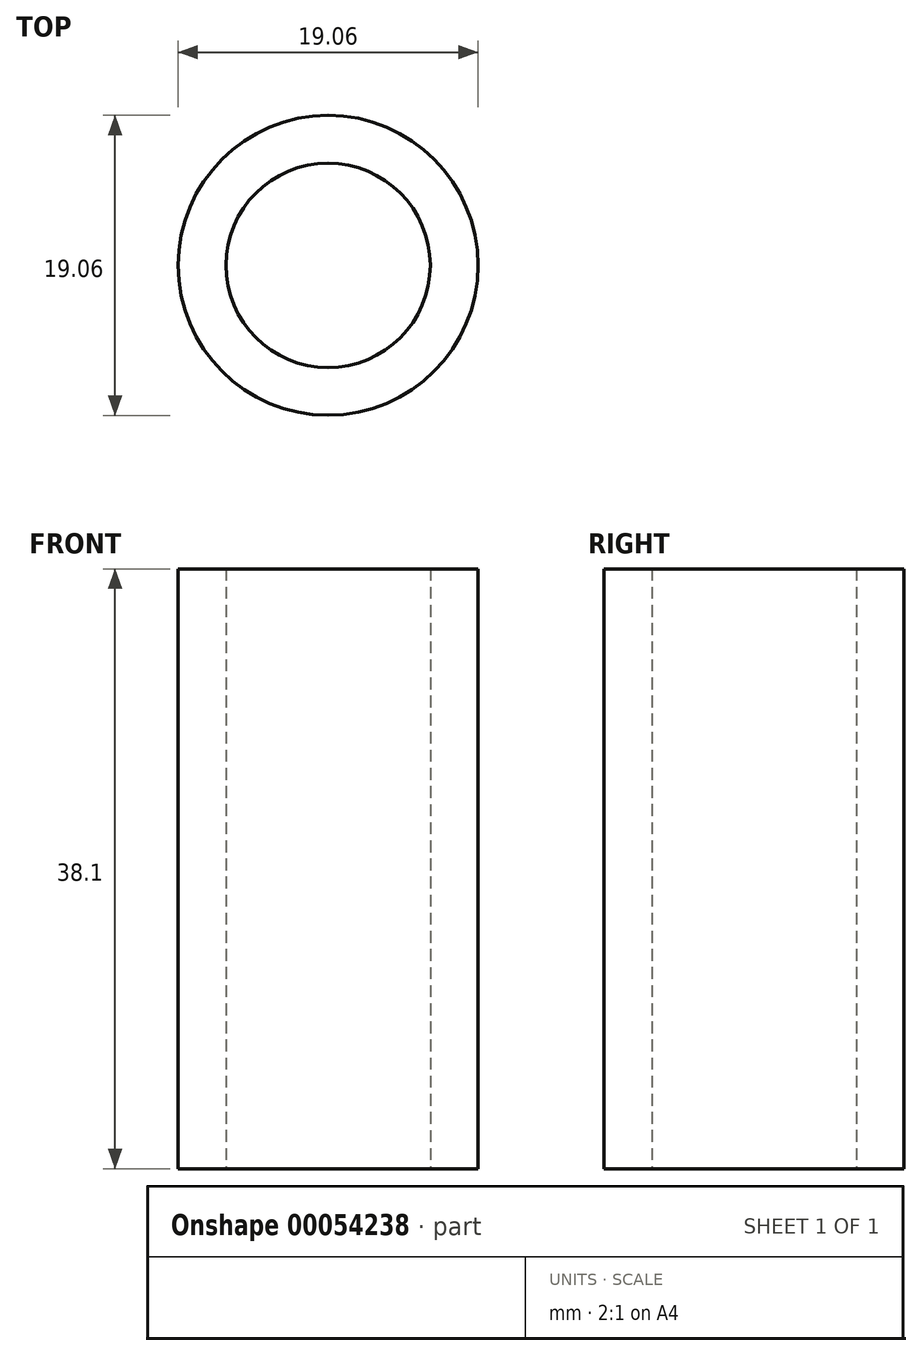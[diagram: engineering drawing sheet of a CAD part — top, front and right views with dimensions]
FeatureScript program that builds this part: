
annotation { "Feature Type Name" : "Feature", "Feature Type Description" : "" }
export const myFeature = defineFeature(function(context is Context, id is Id, definition is map)
    precondition{}
    {
        {
            var Q0;
            Q0=qCreatedBy(makeId("Top.planeOp"),FACE);
            var sketch = newSketch(context, id + "F0", { "sketchPlane" : qUnion([Q0])});
            skCircle(sketch, "E0", {"center": v(0, 0) * mm, "radius": 9.53 * mm});
            skCircle(sketch, "E1", {"center": v(0, 0) * mm, "radius": 6.49 * mm});
            skSolve(sketch);
        }
        {
            var Q0;
            Q0=makeQuery(id+"F0.imprint","IMPRINT",FACE,{"disambiguationData":[TD([[makeQuery(id+"F0.imprint","IMPRINT",EDGE,{"derivedFrom":sQuery(id+"F0.wireOp",EDGE,"E0")}),1.0]])]});
            extrude(context, id + "F1", {"entities" : qUnion([Q0]), "depth" : 38.1 * mm});
        }
    });
